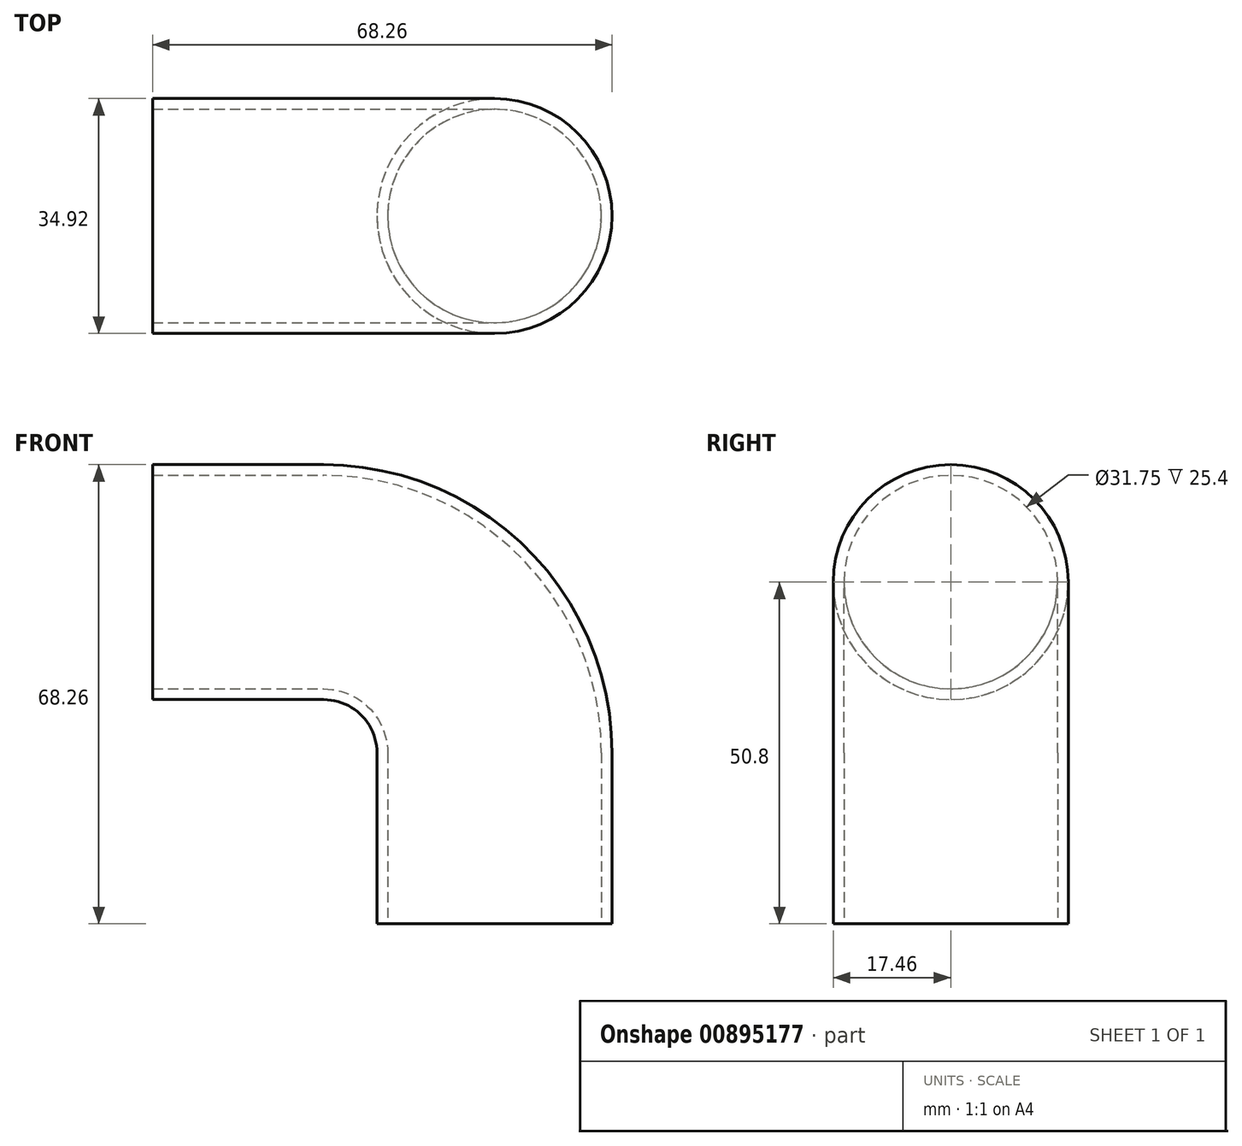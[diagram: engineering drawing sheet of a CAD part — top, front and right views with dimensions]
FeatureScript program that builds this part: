
annotation { "Feature Type Name" : "Feature", "Feature Type Description" : "" }
export const myFeature = defineFeature(function(context is Context, id is Id, definition is map)
    precondition{}
    {
        {
            var Q0;
            Q0=qCreatedBy(makeId("Front.planeOp"),FACE);
            var sketch = newSketch(context, id + "F0", { "sketchPlane" : qUnion([Q0])});
            skLineSegment(sketch, "E0", {"start": v(0, 0) * mm, "end": v(25.4, 0) * mm});
            skLineSegment(sketch, "E1", {"start": v(50.8, -25.4) * mm, "end": v(50.8, -50.8) * mm});
            skPoint(sketch, "E2.visualSharp", {"position": v(50.8, 0) * mm});
            skArc(sketch, "E2.filletArc", {"start": v(50.8, -25.4) * mm, "mid": v(43.36, -7.44) * mm, "end": v(25.4, 0) * mm});
            skSolve(sketch);
        }
        {
            var Q0;
            Q0=qCreatedBy(makeId("Right.planeOp"),FACE);
            var sketch = newSketch(context, id + "F1", { "sketchPlane" : qUnion([Q0])});
            skCircle(sketch, "E3", {"center": v(0, 0) * mm, "radius": 15.88 * mm});
            skCircle(sketch, "E4", {"center": v(0, 0) * mm, "radius": 17.46 * mm});
            skSolve(sketch);
        }
        {
            var Q0;
            Q0=makeQuery(id+"F1.imprint","IMPRINT",FACE,{"disambiguationData":[TD([[makeQuery(id+"F1.imprint","IMPRINT",EDGE,{"derivedFrom":sQuery(id+"F1.wireOp",EDGE,"E3")}),-1.0]])]});
            var Q1;
            Q1=sQuery(id+"F0.wireOp",EDGE,"E0");
            var Q2;
            Q2=sQuery(id+"F0.wireOp",EDGE,"E2.filletArc");
            var Q3;
            Q3=sQuery(id+"F0.wireOp",EDGE,"E1");
            sweep(context, id + "F2", {"profiles" : qUnion([Q0]), "path" : qUnion([Q1, Q2, Q3])});
        }
    });
